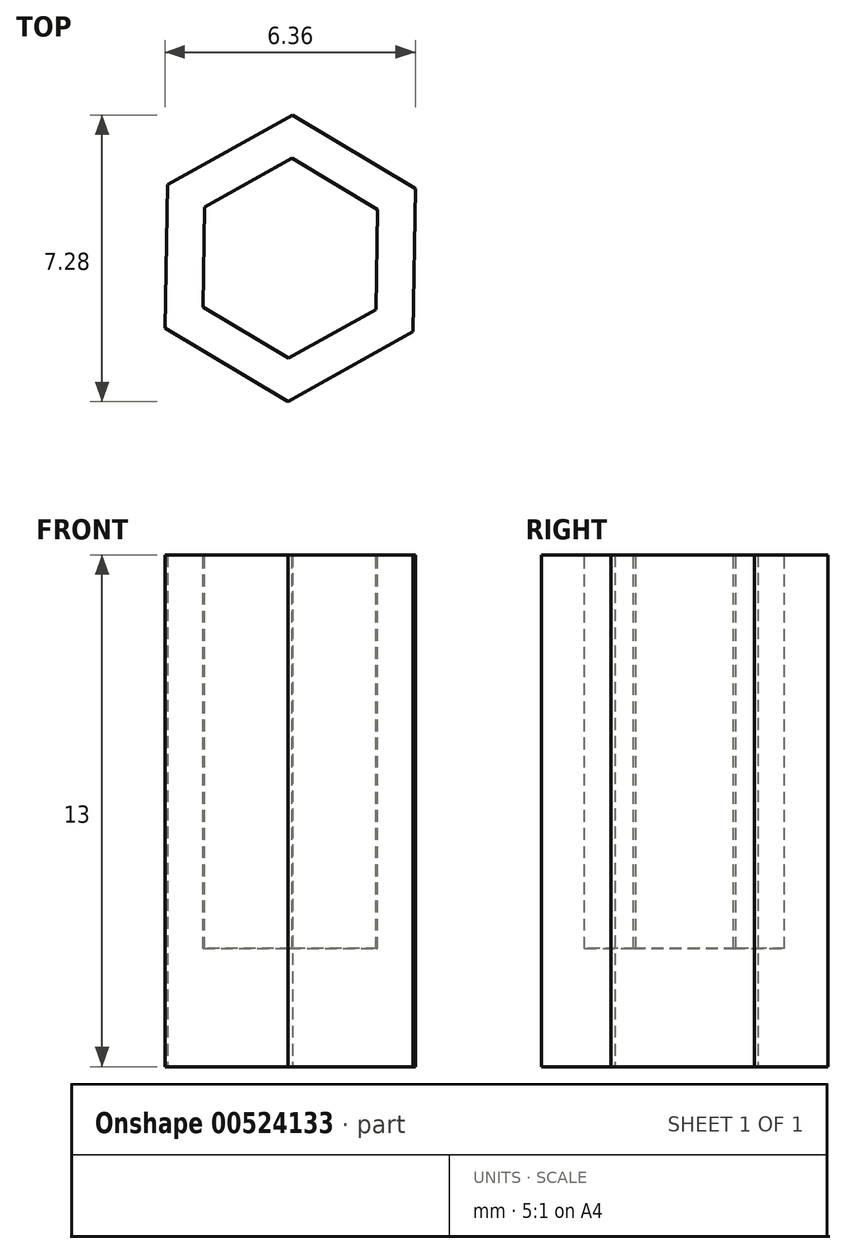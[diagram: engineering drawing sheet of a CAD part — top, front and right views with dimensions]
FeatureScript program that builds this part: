
annotation { "Feature Type Name" : "Feature", "Feature Type Description" : "" }
export const myFeature = defineFeature(function(context is Context, id is Id, definition is map)
    precondition{}
    {
        {
            var Q0;
            Q0=qCreatedBy(makeId("Top.planeOp"),FACE);
            var sketch = newSketch(context, id + "F0", { "sketchPlane" : qUnion([Q0])});
            skCircle(sketch, "E0.cCircle", {"center": v(0, 0) * mm, "radius": 3.64 * mm, "construction": true});
            skLineSegment(sketch, "E0.0", {"start": v(-3.12, 1.87) * mm, "end": v(0.06, 3.64) * mm});
            skLineSegment(sketch, "E0.1", {"start": v(0.06, 3.64) * mm, "end": v(3.18, 1.77) * mm});
            skLineSegment(sketch, "E0.2", {"start": v(3.18, 1.77) * mm, "end": v(3.12, -1.87) * mm});
            skLineSegment(sketch, "E0.3", {"start": v(3.12, -1.87) * mm, "end": v(-0.06, -3.64) * mm});
            skLineSegment(sketch, "E0.4", {"start": v(-0.06, -3.64) * mm, "end": v(-3.18, -1.77) * mm});
            skLineSegment(sketch, "E0.5", {"start": v(-3.18, -1.77) * mm, "end": v(-3.12, 1.87) * mm});
            skSolve(sketch);
        }
        {
            var Q0;
            Q0=makeQuery(id+"F0.imprint","IMPRINT",FACE,{"disambiguationData":[TD([[makeQuery(id+"F0.imprint","IMPRINT",EDGE,{"derivedFrom":sQuery(id+"F0.wireOp",EDGE,"E0.0")}),-1.0]])]});
            extrude(context, id + "F1", {"entities" : qUnion([Q0]), "depth" : 13 * mm, "offsetDistance" : 25 * mm});
        }
        {
            var Q0;
            Q0=makeQuery(id+"F1.opExtrude","CAP_FACE",FACE,{"disambiguationData":[OSD([sQuery(id+"F0.wireOp",EDGE,"E0.0"),sQuery(id+"F0.wireOp",EDGE,"E0.1"),sQuery(id+"F0.wireOp",EDGE,"E0.2"),sQuery(id+"F0.wireOp",EDGE,"E0.3"),sQuery(id+"F0.wireOp",EDGE,"E0.4"),sQuery(id+"F0.wireOp",EDGE,"E0.5")])],"isStart":false});
            var sketch = newSketch(context, id + "F2", { "sketchPlane" : qUnion([Q0])});
            skLineSegment(sketch, "E1.0", {"start": v(0.04, 2.54) * mm, "end": v(-2.18, 1.3) * mm});
            skLineSegment(sketch, "E1.1", {"start": v(-2.22, -1.24) * mm, "end": v(-0.04, -2.54) * mm});
            skLineSegment(sketch, "E1.2", {"start": v(-0.04, -2.54) * mm, "end": v(2.18, -1.3) * mm});
            skLineSegment(sketch, "E1.3", {"start": v(-2.18, 1.3) * mm, "end": v(-2.22, -1.24) * mm});
            skLineSegment(sketch, "E1.4", {"start": v(2.18, -1.3) * mm, "end": v(2.22, 1.24) * mm});
            skLineSegment(sketch, "E1.5", {"start": v(2.22, 1.24) * mm, "end": v(0.04, 2.54) * mm});
            skSolve(sketch);
        }
        {
            var Q0;
            Q0=makeQuery(id+"F2.imprint","IMPRINT",FACE,{"disambiguationData":[TD([[makeQuery(id+"F2.imprint","IMPRINT",EDGE,{"derivedFrom":sQuery(id+"F2.wireOp",EDGE,"E1.0")}),1.0]])]});
            extrude(context, id + "F3", {"entities" : qUnion([Q0]), "operationType" : NewBodyOperationType.REMOVE, "oppositeDirection" : true, "depth" : 10 * mm, "offsetDistance" : 25 * mm});
        }
    });
